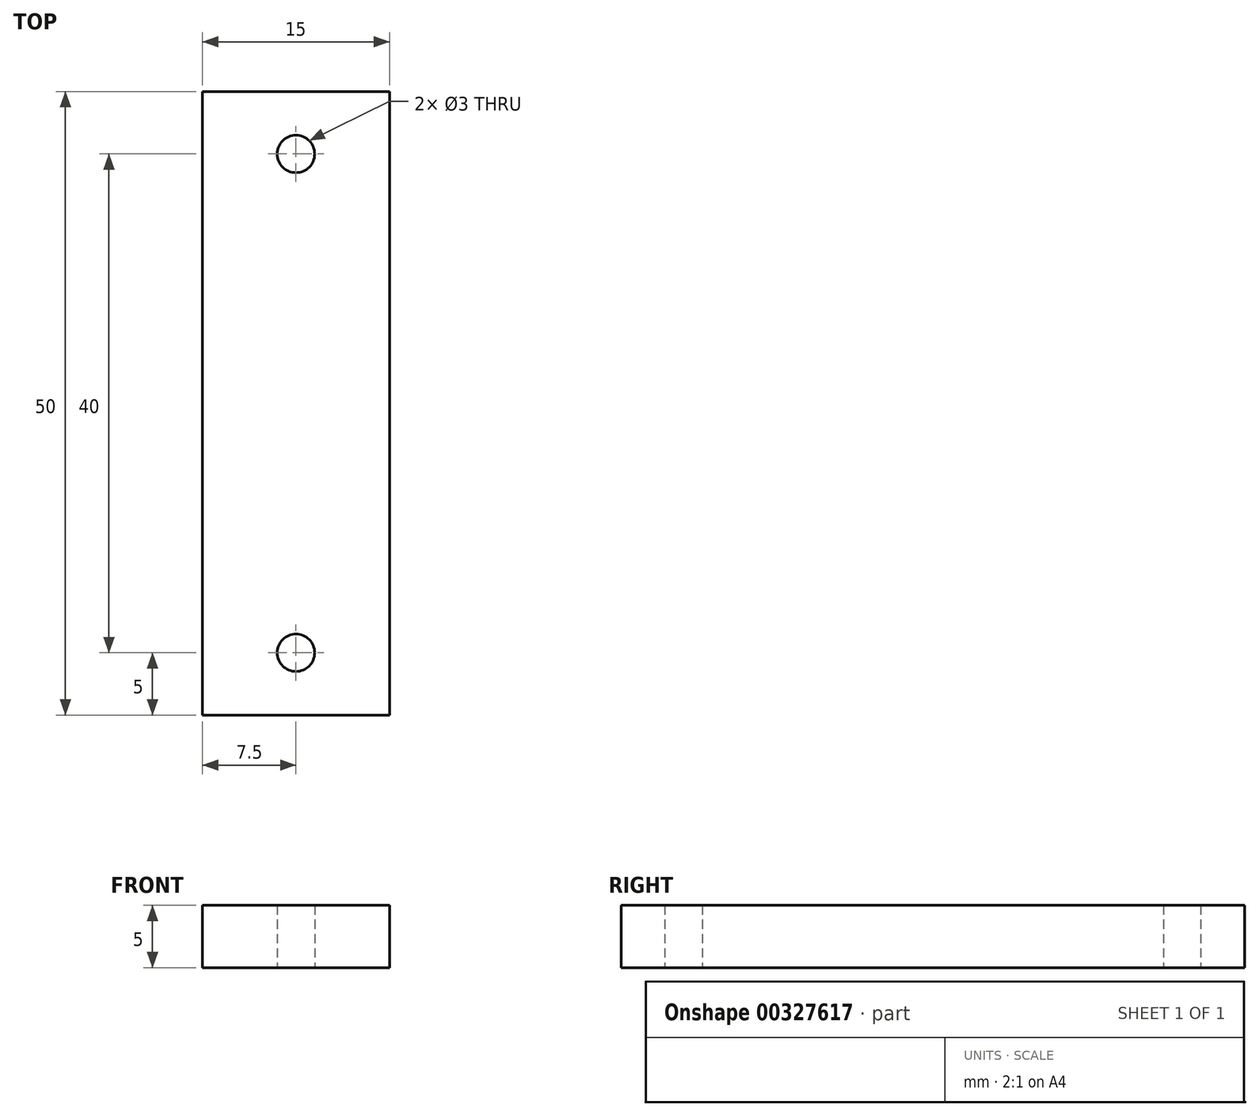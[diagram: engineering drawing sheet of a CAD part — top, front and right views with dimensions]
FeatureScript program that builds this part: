
annotation { "Feature Type Name" : "Feature", "Feature Type Description" : "" }
export const myFeature = defineFeature(function(context is Context, id is Id, definition is map)
    precondition{}
    {
        {
            var Q0;
            Q0=qCreatedBy(makeId("Top.planeOp"),FACE);
            var sketch = newSketch(context, id + "F0", { "sketchPlane" : qUnion([Q0])});
            skLineSegment(sketch, "E0.bottom", {"start": v(0, 0) * mm, "end": v(15, 0) * mm});
            skLineSegment(sketch, "E0.top", {"start": v(0, 50) * mm, "end": v(15, 50) * mm});
            skLineSegment(sketch, "E0.left", {"start": v(0, 0) * mm, "end": v(0, 50) * mm});
            skLineSegment(sketch, "E0.right", {"start": v(15, 0) * mm, "end": v(15, 50) * mm});
            skSolve(sketch);
        }
        {
            var Q0;
            Q0 = qSketchRegion(id + "F0", true);
            extrude(context, id + "F1", {"entities" : qUnion([Q0]), "depth" : 5 * mm});
        }
        {
            var Q0;
            Q0=qCreatedBy(makeId("Top.planeOp"),FACE);
            var sketch = newSketch(context, id + "F2", { "sketchPlane" : qUnion([Q0])});
            skCircle(sketch, "E1", {"center": v(7.5, 45) * mm, "radius": 1.5 * mm});
            skCircle(sketch, "E2", {"center": v(7.5, 5) * mm, "radius": 1.5 * mm});
            skSolve(sketch);
        }
        {
            var Q0;
            Q0 = qSketchRegion(id + "F2", true);
            extrude(context, id + "F3", {"entities" : qUnion([Q0]), "operationType" : NewBodyOperationType.REMOVE, "depth" : 25.4 * mm});
        }
    });
